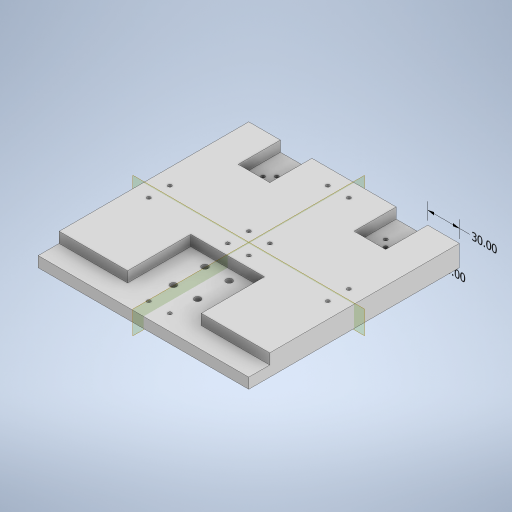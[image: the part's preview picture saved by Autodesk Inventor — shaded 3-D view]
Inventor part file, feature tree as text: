
AUTODESK INVENTOR PART (.ipt)
format: ipt  version: 2023 (Build 270158000, 158)  size: 363,520 bytes
history: native  units: mm
features: sketch x8, extrude x5, other x4, hole x3, plane x2
ambient origin geometry x8: Origin, YZ Plane, XZ Plane, XY Plane, X Axis, Y Axis, Z Axis, Center Point
bodies: Body1 (feature_tree)
feature tree (22):
  other  "Sólido1"
  other  "Anotaciones"
  extrude  "Extrusión1"  Depth=200.0mm
  extrude  "Extrusión2"  Depth=10.0mm TaperAngle=0.0deg
  extrude  "Extrusión3"  Depth=20.0mm
  hole  "Agujero1"  [1 undecoded]
  extrude  "Extrusión4"  Depth=10.0mm
  plane  "Plano de trabajo1"
  plane  "Plano de trabajo2"
  hole  "Agujero2"  [1 undecoded]
  extrude  "Extrusión5"  Depth=10.0mm TaperAngle=0.0deg
  hole  "Agujero3"  [1 undecoded]
  sketch  "Boceto1"  dims[d0=200.0mm d1=200.0mm]
  sketch  "Boceto2"  dims[d2=20.0mm d3=0.0mm]
  sketch  "Boceto3"  dims[d4=20.0mm d5=20.0mm d6=30.0mm d7=30.0mm d8=20.0mm d9=35.0mm d10=35.0mm d11=60.0mm d12=10.0mm d13=0.0mm]
  sketch  "Boceto4"  dims[d14=20.0mm d15=0.0mm]
  sketch  "Boceto5"  dims[d16=3.5mm d18=1.75mm d19=1.75mm d20=1.75mm d21=1.75mm d22=10.0mm d23=10.0mm d25=20.0mm]
  sketch  "Boceto7"  dims[d26=40.0mm d27=40.0mm]
  sketch  "Boceto8"  dims[d28=3.5mm d29=6.0mm d30=4.0mm d31=2.0mm d32=90.0deg d33=8.0mm d34=20.594885mm d38=10.0mm]
  sketch  "Boceto9"  dims[d39=10.0mm d40=40.0mm d41=10.0mm d42=0.0mm d52=3.5mm d54=10.0mm d55=10.0mm d56=3.5mm d57=6.0mm d58=4.0mm d59=2.0mm d60=90.0deg d61=8.0mm d62=20.594885mm d63=32.0mm d64=32.0mm d65=10.0mm d66=0.0mm d67=3.5mm d68=15.0mm d69=10.0mm d70=45.0deg d71=45.0deg d72=3.5mm d73=6.0mm d74=4.0mm d75=2.0mm d76=90.0deg d77=8.0mm d78=20.594885mm d43=6.672192mm d44=4.931866mm d45=30.0mm d46=5.890777mm d47=4.508932mm d48=30.0mm d83=0.5mm d84=0.872665mm d85=0.5mm d86=0.872665mm]
  other  "Cota lineal 1"
  other  "Cota lineal 2"
note: 3 required parameter values undecoded (feature->parameter linkage not recoverable at this tier; creation-order binding heuristic only, values carry confidence <= 0.55)
